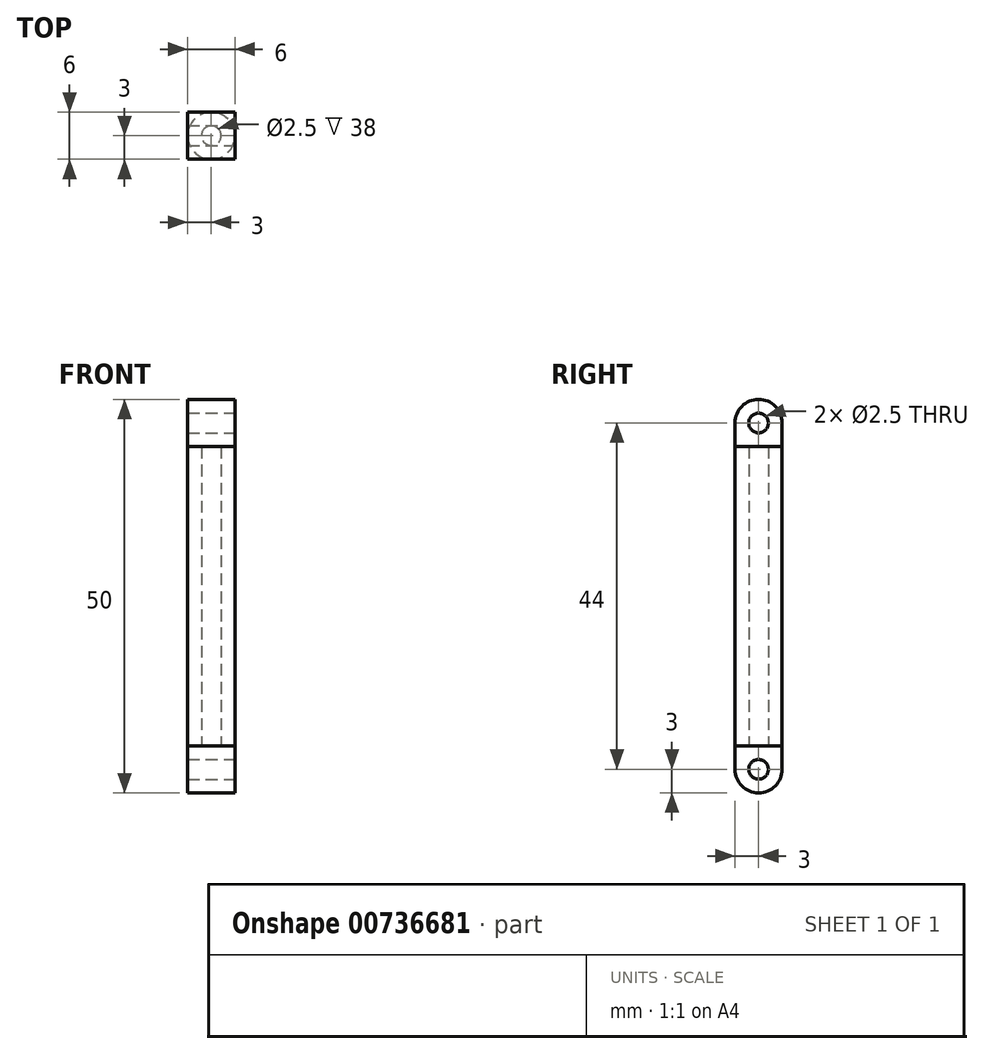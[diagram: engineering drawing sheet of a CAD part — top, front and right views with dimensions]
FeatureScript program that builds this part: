
annotation { "Feature Type Name" : "Feature", "Feature Type Description" : "" }
export const myFeature = defineFeature(function(context is Context, id is Id, definition is map)
    precondition{}
    {
        {
            var Q0;
            Q0=qCreatedBy(makeId("Top.planeOp"),FACE);
            var sketch = newSketch(context, id + "F0", { "sketchPlane" : qUnion([Q0])});
            skCircle(sketch, "E0", {"center": v(0, 0) * mm, "radius": 3 * mm});
            skCircle(sketch, "E1", {"center": v(0, 0) * mm, "radius": 1.25 * mm});
            skLineSegment(sketch, "E2.bottom", {"start": v(-3, -3) * mm, "end": v(3, -3) * mm});
            skLineSegment(sketch, "E2.top", {"start": v(-3, 3) * mm, "end": v(3, 3) * mm});
            skLineSegment(sketch, "E2.left", {"start": v(-3, -3) * mm, "end": v(-3, 3) * mm});
            skLineSegment(sketch, "E2.right", {"start": v(3, -3) * mm, "end": v(3, 3) * mm});
            skSolve(sketch);
        }
        {
            var Q0;
            Q0=makeQuery(id+"F0.imprint","IMPRINT",FACE,{"disambiguationData":[TD([[makeQuery(id+"F0.imprint","IMPRINT",EDGE,{"derivedFrom":sQuery(id+"F0.wireOp",EDGE,"E1")}),-1.0]])]});
            var Q1;
            {var subQ0=sQuery(id+"F0.wireOp",EDGE,"E2.top");var subQ1=sQuery(id+"F0.wireOp",EDGE,"E0");var subQ2=makeQuery(id+"F0.imprint","INTERSECT",VERTEX,{"derivedFrom":[subQ1,subQ0]});Q1=makeQuery(id+"F0.imprint","IMPRINT",FACE,{"disambiguationData":[TD([[makeQuery(id+"F0.imprint","IMPRINT",EDGE,{"disambiguationData":[TD([[subQ2,-1.0]])],"derivedFrom":subQ1}),-1.0]])]});}
            var Q2;
            {var subQ0=sQuery(id+"F0.wireOp",EDGE,"E2.left");var subQ1=sQuery(id+"F0.wireOp",EDGE,"E0");var subQ2=makeQuery(id+"F0.imprint","INTERSECT",VERTEX,{"derivedFrom":[subQ1,subQ0]});Q2=makeQuery(id+"F0.imprint","IMPRINT",FACE,{"disambiguationData":[TD([[makeQuery(id+"F0.imprint","IMPRINT",EDGE,{"disambiguationData":[TD([[subQ2,-1.0]])],"derivedFrom":subQ1}),-1.0]])]});}
            var Q3;
            {var subQ0=sQuery(id+"F0.wireOp",EDGE,"E2.right");var subQ1=sQuery(id+"F0.wireOp",EDGE,"E0");var subQ2=makeQuery(id+"F0.imprint","INTERSECT",VERTEX,{"derivedFrom":[subQ1,subQ0]});Q3=makeQuery(id+"F0.imprint","IMPRINT",FACE,{"disambiguationData":[TD([[makeQuery(id+"F0.imprint","IMPRINT",EDGE,{"disambiguationData":[TD([[subQ2,1.0]])],"derivedFrom":subQ1}),-1.0]])]});}
            var Q4;
            {var subQ0=sQuery(id+"F0.wireOp",EDGE,"E2.top");var subQ1=sQuery(id+"F0.wireOp",EDGE,"E0");var subQ2=makeQuery(id+"F0.imprint","INTERSECT",VERTEX,{"derivedFrom":[subQ1,subQ0]});Q4=makeQuery(id+"F0.imprint","IMPRINT",FACE,{"disambiguationData":[TD([[makeQuery(id+"F0.imprint","IMPRINT",EDGE,{"disambiguationData":[TD([[subQ2,1.0]])],"derivedFrom":subQ1}),-1.0]])]});}
            var Q5;
            {var subQ0=sQuery(id+"F0.wireOp",EDGE,"vyhlab7a-hpru-Pjgy-8969-E8sNITvlcaMQ.bottom");var subQ1=sQuery(id+"F0.wireOp",EDGE,"eWLUR9k0-r7Oy-f8F6-KbXE-X0pT6d8Gba2k");var subQ2=makeQuery(id+"F0.imprint","INTERSECT",VERTEX,{"derivedFrom":[subQ1,subQ0]});Q5=makeQuery(id+"F0.imprint","IMPRINT",FACE,{"disambiguationData":[TD([[makeQuery(id+"F0.imprint","IMPRINT",EDGE,{"disambiguationData":[TD([[subQ2,1.0]])],"derivedFrom":subQ1}),-1.0]])]});}
            var Q6;
            {var subQ0=sQuery(id+"F0.wireOp",EDGE,"vyhlab7a-hpru-Pjgy-8969-E8sNITvlcaMQ.bottom");var subQ1=sQuery(id+"F0.wireOp",EDGE,"eWLUR9k0-r7Oy-f8F6-KbXE-X0pT6d8Gba2k");var subQ2=makeQuery(id+"F0.imprint","INTERSECT",VERTEX,{"derivedFrom":[subQ1,subQ0]});Q6=makeQuery(id+"F0.imprint","IMPRINT",FACE,{"disambiguationData":[TD([[makeQuery(id+"F0.imprint","IMPRINT",EDGE,{"disambiguationData":[TD([[subQ2,-1.0]])],"derivedFrom":subQ1}),-1.0]])]});}
            var Q7;
            Q7=makeQuery(id+"F0.imprint","IMPRINT",FACE,{"disambiguationData":[TD([[makeQuery(id+"F0.imprint","IMPRINT",EDGE,{"derivedFrom":sQuery(id+"F0.wireOp",EDGE,"z6m3nC5t-xj1P-JBVo-caV0-Xawl6uQK7lrJ")}),-1.0]])]});
            var Q8;
            {var subQ0=sQuery(id+"F0.wireOp",EDGE,"vyhlab7a-hpru-Pjgy-8969-E8sNITvlcaMQ.left");var subQ1=sQuery(id+"F0.wireOp",EDGE,"eWLUR9k0-r7Oy-f8F6-KbXE-X0pT6d8Gba2k");var subQ2=makeQuery(id+"F0.imprint","INTERSECT",VERTEX,{"derivedFrom":[subQ1,subQ0]});Q8=makeQuery(id+"F0.imprint","IMPRINT",FACE,{"disambiguationData":[TD([[makeQuery(id+"F0.imprint","IMPRINT",EDGE,{"disambiguationData":[TD([[subQ2,-1.0]])],"derivedFrom":subQ1}),-1.0]])]});}
            var Q9;
            {var subQ0=sQuery(id+"F0.wireOp",EDGE,"vyhlab7a-hpru-Pjgy-8969-E8sNITvlcaMQ.right");var subQ1=sQuery(id+"F0.wireOp",EDGE,"eWLUR9k0-r7Oy-f8F6-KbXE-X0pT6d8Gba2k");var subQ2=makeQuery(id+"F0.imprint","INTERSECT",VERTEX,{"derivedFrom":[subQ1,subQ0]});Q9=makeQuery(id+"F0.imprint","IMPRINT",FACE,{"disambiguationData":[TD([[makeQuery(id+"F0.imprint","IMPRINT",EDGE,{"disambiguationData":[TD([[subQ2,1.0]])],"derivedFrom":subQ1}),-1.0]])]});}
            var Q10;
            Q10=makeQuery(id+"F0.imprint","IMPRINT",FACE,{"disambiguationData":[TD([[makeQuery(id+"F0.imprint","IMPRINT",EDGE,{"derivedFrom":sQuery(id+"F0.wireOp",EDGE,"E1")}),1.0]])]});
            extrude(context, id + "F1", {"entities" : qUnion([Q0, Q1, Q2, Q3, Q4, Q5, Q6, Q7, Q8, Q9, Q10]), "depth" : 6 * mm, "offsetDistance" : 25 * mm});
        }
        {
            var Q0;
            Q0=makeQuery(id+"F0.imprint","IMPRINT",FACE,{"disambiguationData":[TD([[makeQuery(id+"F0.imprint","IMPRINT",EDGE,{"derivedFrom":sQuery(id+"F0.wireOp",EDGE,"E1")}),-1.0]])]});
            extrude(context, id + "F2", {"entities" : qUnion([Q0]), "operationType" : NewBodyOperationType.ADD, "depth" : 44 * mm, "offsetDistance" : 25 * mm});
        }
        {
            var Q0;
            Q0=makeQuery(id+"F1.opExtrude","SWEPT_FACE",FACE,{"disambiguationData":[OSD([sQuery(id+"F0.wireOp",EDGE,"E2.right")])]});
            var sketch = newSketch(context, id + "F3", { "sketchPlane" : qUnion([Q0])});
            skCircle(sketch, "E3", {"center": v(0, 3) * mm, "radius": 1.25 * mm});
            skPoint(sketch, "E3.centerSnap0", {"position": v(-3, 3) * mm});
            skCircle(sketch, "E4", {"center": v(0, 3) * mm, "radius": 3 * mm});
            skSolve(sketch);
        }
        {
            var Q0;
            Q0=makeQuery(id+"F3.imprint","IMPRINT",FACE,{"disambiguationData":[TD([[makeQuery(id+"F3.imprint","IMPRINT",EDGE,{"derivedFrom":sQuery(id+"F3.wireOp",EDGE,"E3")}),1.0]])]});
            var Q1;
            {var subQ0=sQuery(id+"F3.wireOp",EDGE,"E4");var subQ1=sQuery(id+"F0.wireOp",EDGE,"E2.right");var subQ4=makeQuery(id+"F1.opExtrude","CAP_EDGE",EDGE,{"disambiguationData":[OSD([subQ1])],"isStart":true});var subQ5=makeQuery(id+"F3.imprint","INTERSECT",VERTEX,{"derivedFrom":[subQ4,subQ0]});Q1=makeQuery(id+"F3.imprint","IMPRINT",FACE,{"disambiguationData":[TD([[makeQuery(id+"F3.imprint","IMPRINT",EDGE,{"disambiguationData":[TD([[subQ5,1.0]])],"derivedFrom":subQ0}),-1.0]])]});}
            var Q2;
            {var subQ0=sQuery(id+"F3.wireOp",EDGE,"E4");var subQ1=sQuery(id+"F0.wireOp",EDGE,"E2.right");var subQ4=makeQuery(id+"F1.opExtrude","CAP_EDGE",EDGE,{"disambiguationData":[OSD([subQ1])],"isStart":true});var subQ5=makeQuery(id+"F3.imprint","INTERSECT",VERTEX,{"derivedFrom":[subQ4,subQ0]});Q2=makeQuery(id+"F3.imprint","IMPRINT",FACE,{"disambiguationData":[TD([[makeQuery(id+"F3.imprint","IMPRINT",EDGE,{"disambiguationData":[TD([[subQ5,-1.0]])],"derivedFrom":subQ0}),-1.0]])]});}
            extrude(context, id + "F4", {"entities" : qUnion([Q0, Q1, Q2]), "operationType" : NewBodyOperationType.REMOVE, "oppositeDirection" : true, "depth" : 6 * mm, "offsetDistance" : 25 * mm});
        }
        {
            var Q0;
            Q0=makeQuery(id+"F2.opExtrude","CAP_FACE",FACE,{"disambiguationData":[OSD([sQuery(id+"F0.wireOp",EDGE,"E0"),sQuery(id+"F0.wireOp",EDGE,"E1")])],"isStart":false});
            var sketch = newSketch(context, id + "F5", { "sketchPlane" : qUnion([Q0])});
            skLineSegment(sketch, "E5.bottom", {"start": v(-3, 3) * mm, "end": v(3, 3) * mm});
            skLineSegment(sketch, "E5.top", {"start": v(-3, -3) * mm, "end": v(3, -3) * mm});
            skLineSegment(sketch, "E5.left", {"start": v(-3, 3) * mm, "end": v(-3, -3) * mm});
            skLineSegment(sketch, "E5.right", {"start": v(3, 3) * mm, "end": v(3, -3) * mm});
            skSolve(sketch);
        }
        {
            var Q0;
            Q0 = qSketchRegion(id + "F5", true);
            extrude(context, id + "F6", {"entities" : qUnion([Q0]), "operationType" : NewBodyOperationType.ADD, "depth" : 6 * mm, "offsetDistance" : 25 * mm});
        }
        {
            var Q0;
            Q0=makeQuery(id+"F6.opExtrude","SWEPT_FACE",FACE,{"disambiguationData":[OSD([sQuery(id+"F5.wireOp",EDGE,"E5.right")])]});
            var sketch = newSketch(context, id + "F7", { "sketchPlane" : qUnion([Q0])});
            skCircle(sketch, "E6", {"center": v(0, 47) * mm, "radius": 1.25 * mm});
            skPoint(sketch, "E6.centerSnap0", {"position": v(3, 47) * mm});
            skCircle(sketch, "E7", {"center": v(0, 47) * mm, "radius": 3 * mm});
            skSolve(sketch);
        }
        {
            var Q0;
            Q0=makeQuery(id+"F7.imprint","IMPRINT",FACE,{"disambiguationData":[TD([[makeQuery(id+"F7.imprint","IMPRINT",EDGE,{"derivedFrom":sQuery(id+"F7.wireOp",EDGE,"E6")}),1.0]])]});
            var Q1;
            {var subQ0=sQuery(id+"F7.wireOp",EDGE,"E7");var subQ1=sQuery(id+"F5.wireOp",EDGE,"E5.right");var subQ2=makeQuery(id+"F6.opExtrude","CAP_EDGE",EDGE,{"disambiguationData":[OSD([subQ1])],"isStart":false});var subQ3=makeQuery(id+"F7.imprint","INTERSECT",VERTEX,{"derivedFrom":[subQ2,subQ0]});Q1=makeQuery(id+"F7.imprint","IMPRINT",FACE,{"disambiguationData":[TD([[makeQuery(id+"F7.imprint","IMPRINT",EDGE,{"disambiguationData":[TD([[subQ3,-1.0]])],"derivedFrom":subQ0}),-1.0]])]});}
            var Q2;
            {var subQ0=sQuery(id+"F7.wireOp",EDGE,"E7");var subQ1=sQuery(id+"F5.wireOp",EDGE,"E5.right");var subQ2=makeQuery(id+"F6.opExtrude","CAP_EDGE",EDGE,{"disambiguationData":[OSD([subQ1])],"isStart":false});var subQ3=makeQuery(id+"F7.imprint","INTERSECT",VERTEX,{"derivedFrom":[subQ2,subQ0]});Q2=makeQuery(id+"F7.imprint","IMPRINT",FACE,{"disambiguationData":[TD([[makeQuery(id+"F7.imprint","IMPRINT",EDGE,{"disambiguationData":[TD([[subQ3,1.0]])],"derivedFrom":subQ0}),-1.0]])]});}
            extrude(context, id + "F8", {"entities" : qUnion([Q0, Q1, Q2]), "operationType" : NewBodyOperationType.REMOVE, "oppositeDirection" : true, "depth" : 25 * mm, "offsetDistance" : 25 * mm});
        }
    });
